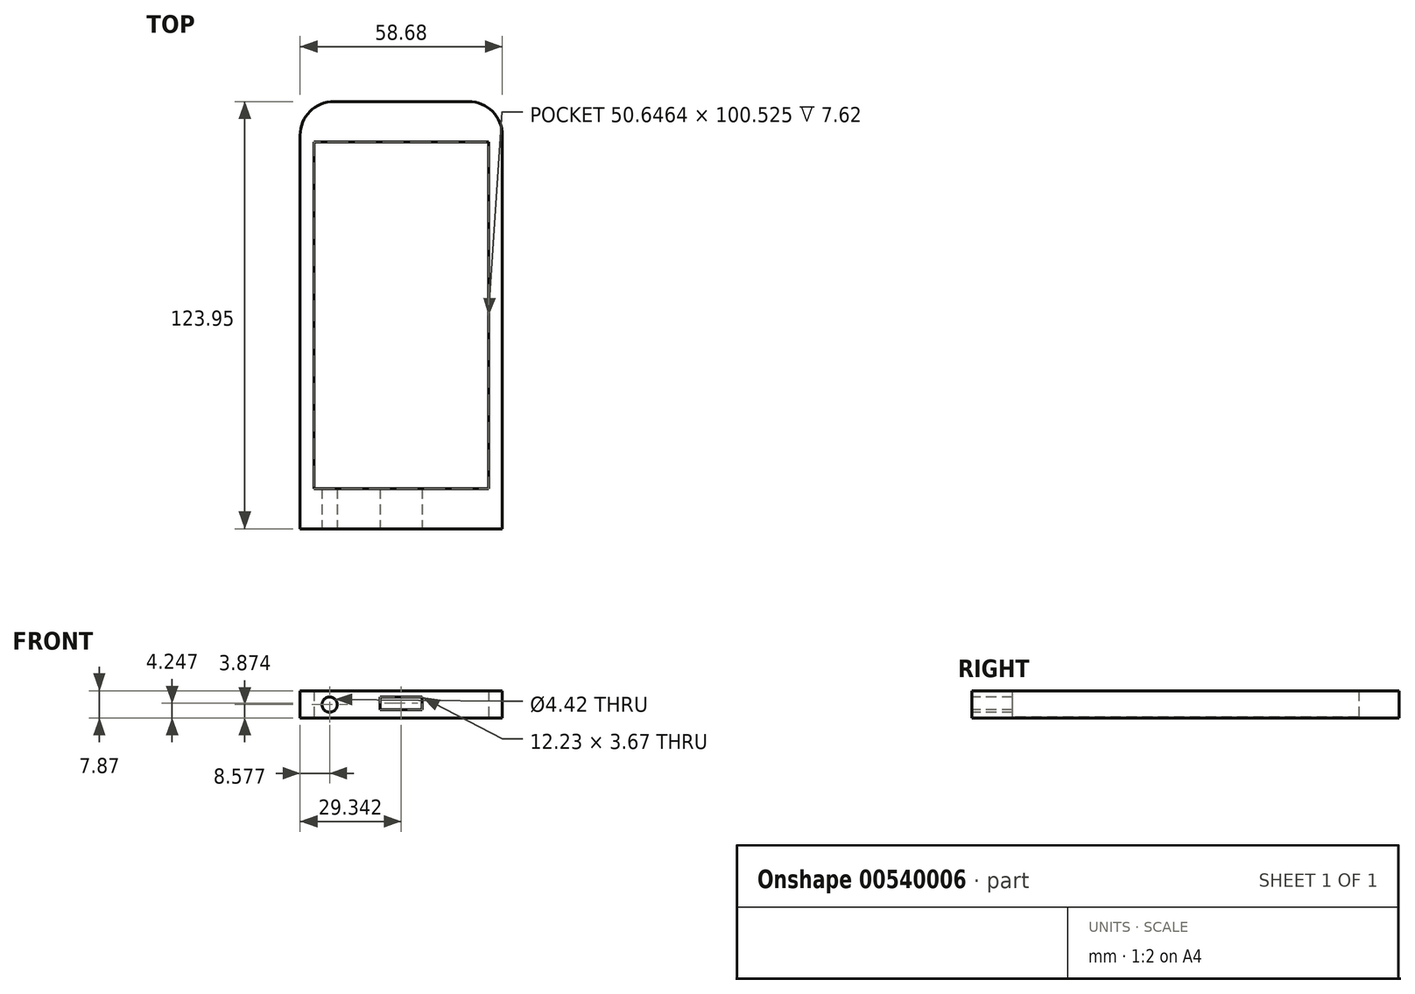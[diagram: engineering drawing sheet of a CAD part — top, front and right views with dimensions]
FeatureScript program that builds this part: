
annotation { "Feature Type Name" : "Feature", "Feature Type Description" : "" }
export const myFeature = defineFeature(function(context is Context, id is Id, definition is map)
    precondition{}
    {
        {
            var Q0;
            Q0=qCreatedBy(makeId("Top.planeOp"),FACE);
            var sketch = newSketch(context, id + "F0", { "sketchPlane" : qUnion([Q0])});
            skLineSegment(sketch, "E0.bottom", {"start": v(26.48, 116.92) * mm, "end": v(85.16, 116.92) * mm});
            skLineSegment(sketch, "E0.top", {"start": v(26.48, -7.03) * mm, "end": v(85.16, -7.03) * mm});
            skLineSegment(sketch, "E0.left", {"start": v(26.48, 116.92) * mm, "end": v(26.48, -7.03) * mm});
            skLineSegment(sketch, "E0.right", {"start": v(85.16, 116.92) * mm, "end": v(85.16, -7.03) * mm});
            skPoint(sketch, "E0.middle", {"position": v(55.82, 54.94) * mm});
            skLineSegment(sketch, "E1.bottom", {"start": v(30.5, 105.2) * mm, "end": v(81.14, 105.2) * mm});
            skLineSegment(sketch, "E1.top", {"start": v(30.5, 4.68) * mm, "end": v(81.14, 4.68) * mm});
            skLineSegment(sketch, "E1.left", {"start": v(30.5, 105.2) * mm, "end": v(30.5, 4.68) * mm});
            skLineSegment(sketch, "E1.right", {"start": v(81.14, 105.2) * mm, "end": v(81.14, 4.68) * mm});
            skSolve(sketch);
        }
        {
            var Q0;
            Q0=makeQuery(id+"F0.imprint","IMPRINT",FACE,{"disambiguationData":[TD([[makeQuery(id+"F0.imprint","IMPRINT",EDGE,{"derivedFrom":sQuery(id+"F0.wireOp",EDGE,"E1.bottom")}),-1.0]])]});
            extrude(context, id + "F1", {"entities" : qUnion([Q0]), "depth" : 0.25 * mm, "offsetDistance" : 25.4 * mm});
        }
        {
            var Q0;
            Q0=makeQuery(id+"F0.imprint","IMPRINT",FACE,{"disambiguationData":[TD([[makeQuery(id+"F0.imprint","IMPRINT",EDGE,{"derivedFrom":sQuery(id+"F0.wireOp",EDGE,"E0.bottom")}),-1.0]])]});
            extrude(context, id + "F2", {"entities" : qUnion([Q0]), "operationType" : NewBodyOperationType.ADD, "depth" : 7.87 * mm, "offsetDistance" : 25.4 * mm});
        }
        {
            var Q0;
            Q0=makeQuery(id+"F2.opExtrude","SWEPT_EDGE",EDGE,{"disambiguationData":[OSD([sQuery(id+"F0.wireOp",EDGE,"E0.bottom"),sQuery(id+"F0.wireOp",EDGE,"E0.left")])]});
            fillet(context, id + "F3", {"entities" : qUnion([Q0]), "radius" : 9.8 * mm, "tangentPropagation" : true, "allowEdgeOverflow" : false});
        }
        {
            var Q0;
            Q0=makeQuery(id+"F2.opExtrude","SWEPT_EDGE",EDGE,{"disambiguationData":[OSD([sQuery(id+"F0.wireOp",EDGE,"E0.bottom"),sQuery(id+"F0.wireOp",EDGE,"E0.right")])]});
            fillet(context, id + "F4", {"entities" : qUnion([Q0]), "radius" : 9.8 * mm, "tangentPropagation" : true, "allowEdgeOverflow" : false});
        }
        {
            var Q0;
            Q0=sQuery(id+"F0.wireOp",EDGE,"E1.bottom");
            extrude(context, id + "F5", {"bodyType" : ToolBodyType.SURFACE, "surfaceEntities" : qUnion([Q0]), "depth" : 2.03 * mm, "offsetDistance" : 25.4 * mm});
        }
        {
            var Q0;
            Q0=makeQuery(id+"F2.opExtrude","SWEPT_FACE",FACE,{"disambiguationData":[OSD([sQuery(id+"F0.wireOp",EDGE,"E0.top")])]});
            var sketch = newSketch(context, id + "F6", { "sketchPlane" : qUnion([Q0])});
            skLineSegment(sketch, "E2.bottom", {"start": v(49.7, 2.41) * mm, "end": v(61.94, 2.41) * mm});
            skLineSegment(sketch, "E2.top", {"start": v(49.7, 6.08) * mm, "end": v(61.94, 6.08) * mm});
            skLineSegment(sketch, "E2.left", {"start": v(49.7, 2.41) * mm, "end": v(49.7, 6.08) * mm});
            skLineSegment(sketch, "E2.right", {"start": v(61.94, 2.41) * mm, "end": v(61.94, 6.08) * mm});
            skPoint(sketch, "E2.middle", {"position": v(55.82, 4.25) * mm});
            skPoint(sketch, "E2.middle.positionSnap0", {"position": v(55.82, 7.87) * mm});
            skPoint(sketch, "E2.centerSnap0", {"position": v(55.82, 7.87) * mm});
            skSolve(sketch);
        }
        {
            var Q0;
            Q0=makeQuery(id+"F6.imprint","IMPRINT",FACE,{"disambiguationData":[TD([[makeQuery(id+"F6.imprint","IMPRINT",EDGE,{"derivedFrom":sQuery(id+"F6.wireOp",EDGE,"E2.bottom")}),1.0]])]});
            extrude(context, id + "F7", {"entities" : qUnion([Q0]), "operationType" : NewBodyOperationType.REMOVE, "oppositeDirection" : true, "depth" : 17.27 * mm, "offsetDistance" : 25.4 * mm});
        }
        {
            var Q0;
            Q0=makeQuery(id+"F2.opExtrude","SWEPT_FACE",FACE,{"disambiguationData":[OSD([sQuery(id+"F0.wireOp",EDGE,"E0.top")])]});
            var sketch = newSketch(context, id + "F8", { "sketchPlane" : qUnion([Q0])});
            skCircle(sketch, "E3", {"center": v(35.06, 3.87) * mm, "radius": 2.21 * mm});
            skSolve(sketch);
        }
        {
            var Q0;
            Q0=makeQuery(id+"F8.imprint","IMPRINT",FACE,{"disambiguationData":[TD([[makeQuery(id+"F8.imprint","IMPRINT",EDGE,{"derivedFrom":sQuery(id+"F8.wireOp",EDGE,"E3")}),1.0]])]});
            extrude(context, id + "F9", {"entities" : qUnion([Q0]), "operationType" : NewBodyOperationType.REMOVE, "oppositeDirection" : true, "depth" : 12.2 * mm, "offsetDistance" : 25.4 * mm});
        }
    });
